# Revit family: Spaces in Between_Comfort
name_source: partatom
category: Furniture
units: mm (PartAtom-declared; Revit-internal decimal feet)

## family parameters
Always vertical = Yes
Cut with Voids When Loaded = No
OmniClass Number = 23.40.20.00
OmniClass Title = General Furniture and Specialties
Room Calculation Point = No
Shared = No
Work Plane-Based = No

## types (1)
- Spaces in Between_Comfort
    3" Rectangle Leg = <By Category>
    6" Rectangle Leg = <By Category>
    Glide = <By Category>
    Linear C-Ottoman Seat Fabric = <By Category>
    Linear C-Ottoman Side Fabric = <By Category>
    Linear Chair Back Fabric - 1 = <By Category>
    Linear Chair Back Fabric - 3 = <By Category>
    Linear Chair Back Fabric -2 = <By Category>
    Linear Chair Seat Fabric - 2 = <By Category>
    Linear Chair Seat Fabric - 3 = <By Category>
    Linear Chair Seat Fabric -1 = <By Category>
    Linear Corner Back Fabric - 1 = <By Category>
    Linear Corner Back Fabric - 2 = <By Category>
    Linear Corner Seat Fabric - 1 = <By Category>
    Linear Corner Seat Fabric - 2 = <By Category>
    Linear Sofa Back Fabric = <By Category>
    Linear Sofa Seat Fabric = <By Category>
    Linear Wedge Seat Fabric - 1 = <By Category>
    Linear Wedge Seat Fabric - 2 = <By Category>
    Linear Wedge Seat Fabric - 3 = <By Category>
    Linear Wedge Seat Fabric - 4 = <By Category>
    Linear Wedge Side Fabric - 1 = <By Category>
    Linear Wedge Side Fabric - 2 = <By Category>
    Linear Wedge Side Fabric - 3 = <By Category>
    Linear Wedge Side Fabric - 4 = <By Category>
    Manufacturer = FOMCORE
    Model = Spaces in Between_Comfort
    Round Ottoman Laminate Edge - 1 = <By Category>
    Round Ottoman Laminate Edge - 2 = <By Category>
    Round Ottoman Laminate Top - 1 = <By Category>
    Round Ottoman Laminate Top - 2 = <By Category>
    Round Ottoman Seat Fabric - 1 = <By Category>
    Round Ottoman Seat Fabric - 2 = <By Category>
    Round Ottoman Side Fabric - 1 = <By Category>
    Round Ottoman Side Fabric - 2 = <By Category>
    Sled Leg29 = <By Category>
    Triangle Leg = <By Category>
    Type Comments = COMBO UNIT
    URL = https://fomcore.com

## geometry (parser evidence)
native form markers: Sweep x7
no freeform markers — native parametric forms only
